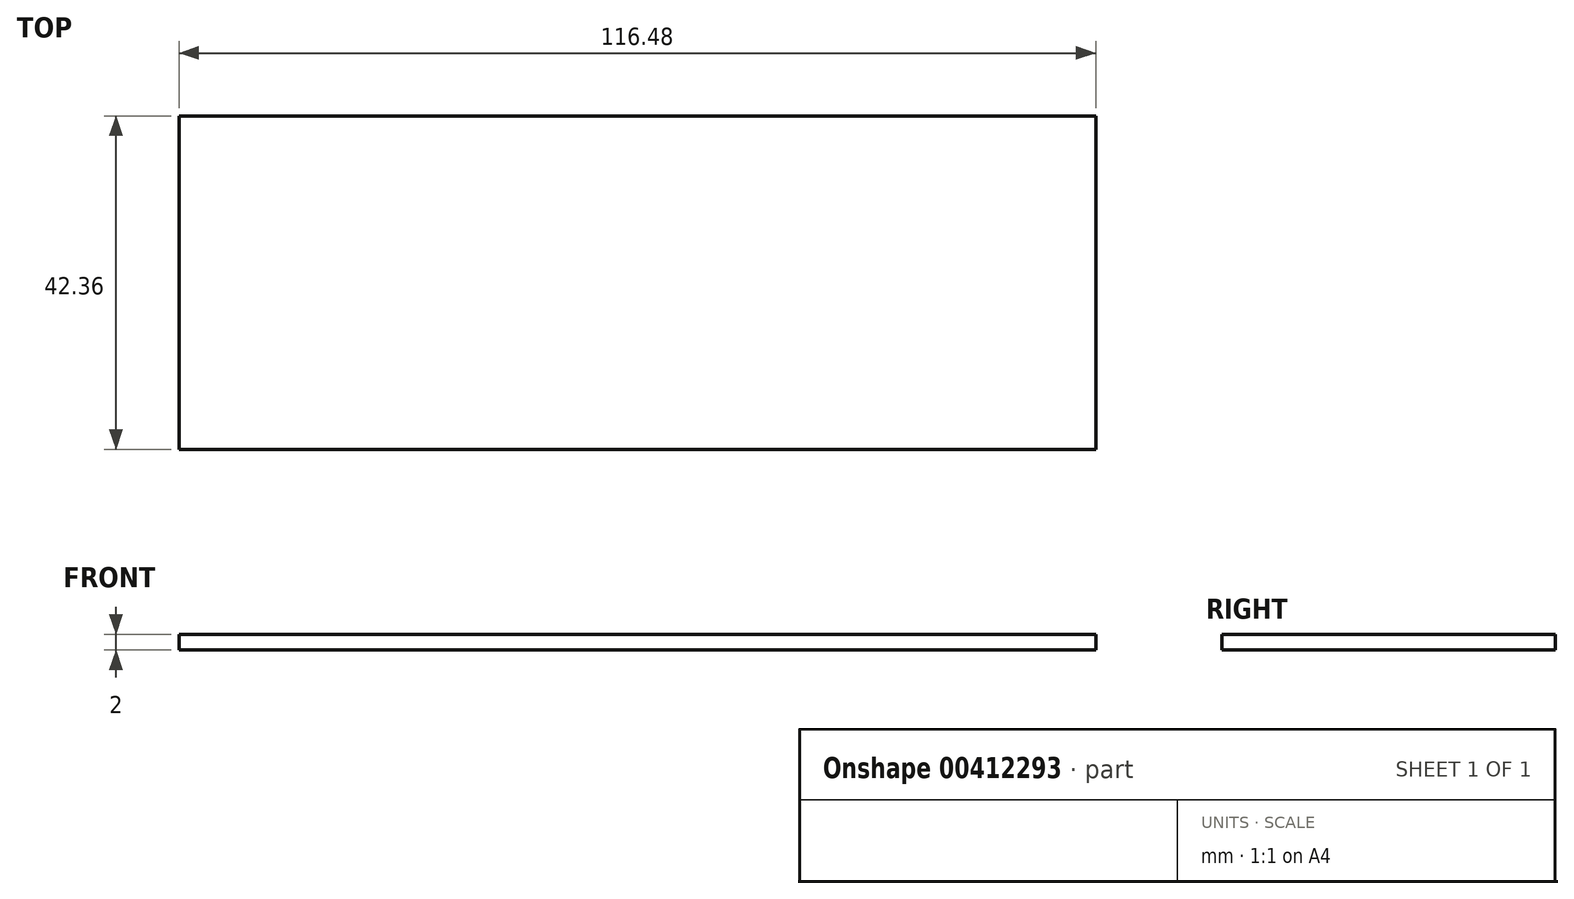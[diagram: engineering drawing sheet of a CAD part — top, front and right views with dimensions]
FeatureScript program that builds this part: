
annotation { "Feature Type Name" : "Feature", "Feature Type Description" : "" }
export const myFeature = defineFeature(function(context is Context, id is Id, definition is map)
    precondition{}
    {
        {
            var Q0;
            Q0=qCreatedBy(makeId("Top.planeOp"),FACE);
            var sketch = newSketch(context, id + "F0", { "sketchPlane" : qUnion([Q0])});
            skLineSegment(sketch, "E0.bottom", {"start": v(-58.24, -23.53) * mm, "end": v(58.24, -23.53) * mm});
            skLineSegment(sketch, "E0.top", {"start": v(-58.24, 18.83) * mm, "end": v(58.24, 18.83) * mm});
            skLineSegment(sketch, "E0.left", {"start": v(-58.24, -23.53) * mm, "end": v(-58.24, 18.83) * mm});
            skLineSegment(sketch, "E0.right", {"start": v(58.24, -23.53) * mm, "end": v(58.24, 18.83) * mm});
            skPoint(sketch, "E0.middle", {"position": v(0, -2.35) * mm});
            skSolve(sketch);
        }
        {
            var Q0;
            Q0=makeQuery(id+"F0.imprint","IMPRINT",FACE,{"disambiguationData":[TD([[makeQuery(id+"F0.imprint","IMPRINT",EDGE,{"derivedFrom":sQuery(id+"F0.wireOp",EDGE,"E0.bottom")}),1.0]])]});
            extrude(context, id + "F1", {"entities" : qUnion([Q0]), "depth" : 2 * mm});
        }
    });
